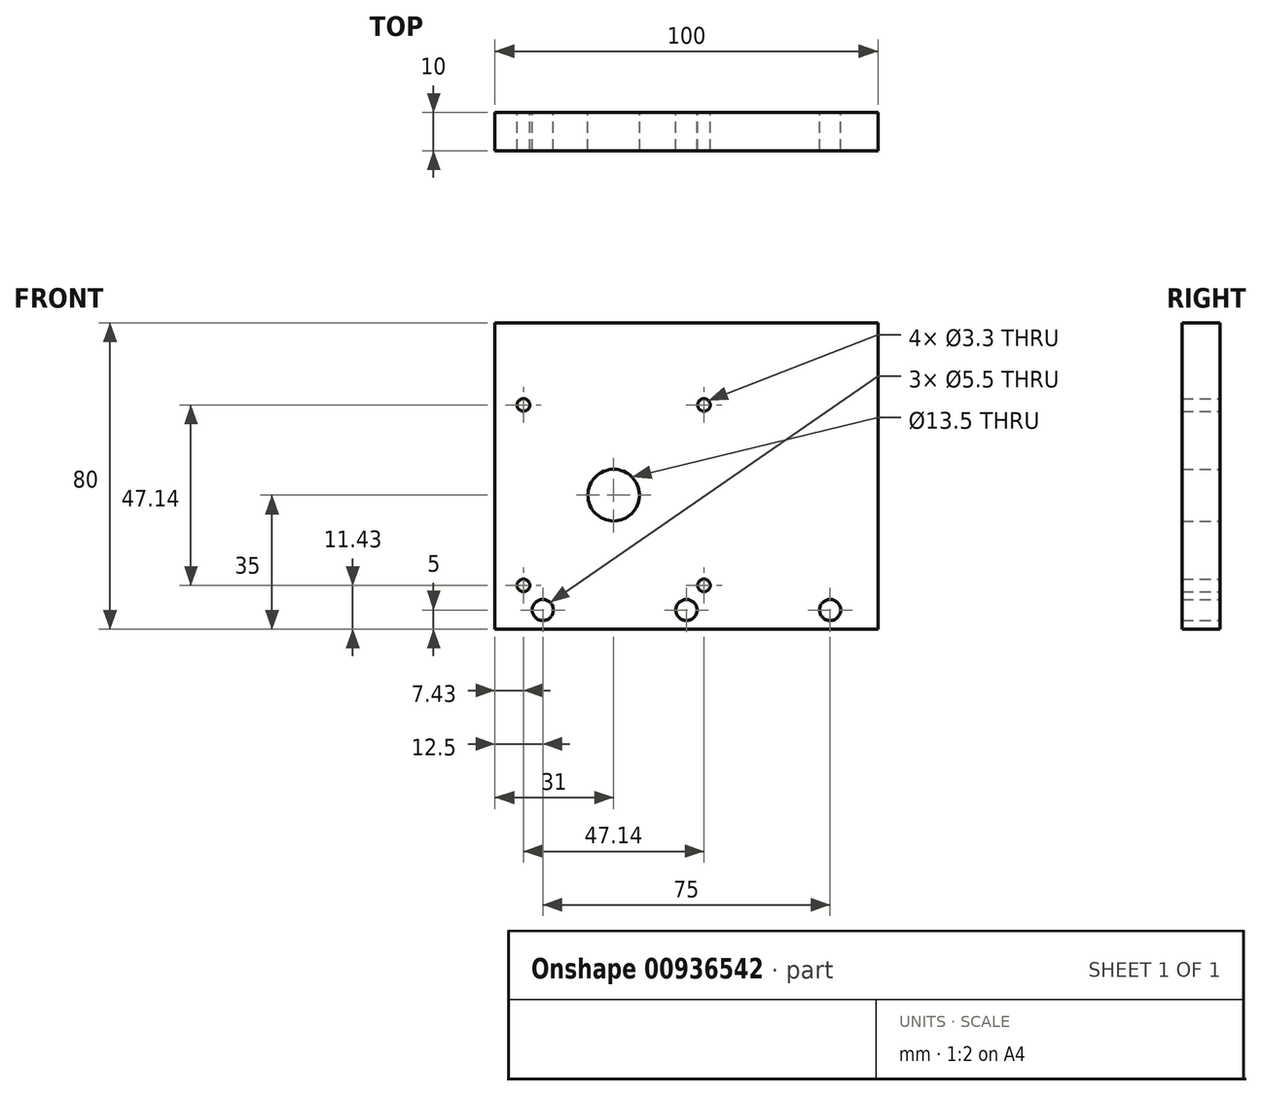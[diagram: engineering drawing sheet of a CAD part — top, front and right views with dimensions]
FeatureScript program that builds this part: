
annotation { "Feature Type Name" : "Feature", "Feature Type Description" : "" }
export const myFeature = defineFeature(function(context is Context, id is Id, definition is map)
    precondition{}
    {
        {
            var Q0;
            Q0=qCreatedBy(makeId("Front.planeOp"),FACE);
            var sketch = newSketch(context, id + "F0", { "sketchPlane" : qUnion([Q0])});
            skLineSegment(sketch, "E0.bottom", {"start": v(50, 40) * mm, "end": v(-50, 40) * mm});
            skLineSegment(sketch, "E0.top", {"start": v(50, -40) * mm, "end": v(-50, -40) * mm});
            skLineSegment(sketch, "E0.left", {"start": v(50, 40) * mm, "end": v(50, -40) * mm});
            skLineSegment(sketch, "E0.right", {"start": v(-50, 40) * mm, "end": v(-50, -40) * mm});
            skPoint(sketch, "E0.middle", {"position": v(0, 0) * mm});
            skSolve(sketch);
        }
        {
            var Q0;
            Q0=makeQuery(id+"F0.imprint","IMPRINT",FACE,{"disambiguationData":[TD([[makeQuery(id+"F0.imprint","IMPRINT",EDGE,{"derivedFrom":sQuery(id+"F0.wireOp",EDGE,"E0.bottom")}),1.0]])]});
            extrude(context, id + "F1", {"entities" : qUnion([Q0]), "depth" : 10 * mm, "offsetDistance" : 25 * mm});
        }
        {
            var Q0;
            Q0=makeQuery(id+"F1.opExtrude","CAP_FACE",FACE,{"disambiguationData":[OSD([sQuery(id+"F0.wireOp",EDGE,"E0.bottom"),sQuery(id+"F0.wireOp",EDGE,"E0.top"),sQuery(id+"F0.wireOp",EDGE,"E0.left"),sQuery(id+"F0.wireOp",EDGE,"E0.right")])],"isStart":false});
            var sketch = newSketch(context, id + "F2", { "sketchPlane" : qUnion([Q0])});
            skLineSegment(sketch, "E1.bottom", {"start": v(4.57, 18.57) * mm, "end": v(-42.57, 18.57) * mm, "construction": true});
            skLineSegment(sketch, "E1.top", {"start": v(4.57, -28.57) * mm, "end": v(-42.57, -28.57) * mm, "construction": true});
            skLineSegment(sketch, "E1.left", {"start": v(4.57, 18.57) * mm, "end": v(4.57, -28.57) * mm, "construction": true});
            skLineSegment(sketch, "E1.right", {"start": v(-42.57, 18.57) * mm, "end": v(-42.57, -28.57) * mm, "construction": true});
            skPoint(sketch, "E1.middle", {"position": v(-19, -5) * mm});
            skPoint(sketch, "E2", {"position": v(4.57, 18.57) * mm});
            skPoint(sketch, "E3", {"position": v(-42.57, 18.57) * mm});
            skPoint(sketch, "E4", {"position": v(-42.57, -28.57) * mm});
            skPoint(sketch, "E5", {"position": v(4.57, -28.57) * mm});
            skLineSegment(sketch, "E6", {"start": v(-50, -35) * mm, "end": v(50, -35) * mm, "construction": true});
            skPoint(sketch, "E7", {"position": v(0, -35) * mm});
            skPoint(sketch, "E8", {"position": v(-37.5, -35) * mm});
            skPoint(sketch, "E9", {"position": v(37.5, -35) * mm});
            skSolve(sketch);
        }
        {
            var Q0;
            Q0=sQuery(id+"F2.wireOp",VERTEX,"E1.bottom.end");
            var Q1;
            Q1=sQuery(id+"F2.wireOp",VERTEX,"E1.bottom.start");
            var Q2;
            Q2=sQuery(id+"F2.wireOp",VERTEX,"E4");
            var Q3;
            Q3=sQuery(id+"F2.wireOp",VERTEX,"E5");
            var Q4;
            Q4=makeQuery(id+"F1.opExtrude","SWEPT_BODY",BODY,{"disambiguationData":[OSD([sQuery(id+"F0.wireOp",EDGE,"E0.bottom"),sQuery(id+"F0.wireOp",EDGE,"E0.top"),sQuery(id+"F0.wireOp",EDGE,"E0.left"),sQuery(id+"F0.wireOp",EDGE,"E0.right")])]});
            hole(context, id + "F3", {"style" : HoleStyle.SIMPLE, "endStyle" : HoleEndStyle.THROUGH, "standardTappedOrClearance" : lookupTablePath({ "standard" : "ISO", "engagement" : "75%", "pitch" : "0.7 mm", "size" : "M4", "type" : "Tapped" }), "standardBlindInLast" : lookupTablePath({ "standard" : "ISO", "fit" : "Normal", "engagement" : "75%", "pitch" : "0.7 mm", "size" : "M4", "type" : "Clearance & tapped" }), "holeDiameter" : 3.3 * mm, "majorDiameter" : 4 * mm, "showTappedDepth" : true, "tappedDepth" : 12 * mm, "tapClearance" : 3, "locations" : qUnion([Q0, Q1, Q2, Q3]), "scope" : qUnion([Q4]), "startStyle" : HoleStartStyle.PART});
        }
        {
            var Q0;
            Q0=sQuery(id+"F2.wireOp",VERTEX,"E1.middle");
            var Q1;
            Q1=makeQuery(id+"F1.opExtrude","SWEPT_BODY",BODY,{"disambiguationData":[OSD([sQuery(id+"F0.wireOp",EDGE,"E0.bottom"),sQuery(id+"F0.wireOp",EDGE,"E0.top"),sQuery(id+"F0.wireOp",EDGE,"E0.left"),sQuery(id+"F0.wireOp",EDGE,"E0.right")])]});
            hole(context, id + "F4", {"style" : HoleStyle.SIMPLE, "endStyle" : HoleEndStyle.THROUGH, "standardTappedOrClearance" : lookupTablePath({ "fit" : "Normal", "standard" : "ISO", "size" : "M12", "type" : "Clearance" }), "standardBlindInLast" : lookupTablePath({ "fit" : "Normal", "standard" : "ISO", "engagement" : "75%", "pitch" : "1.75 mm", "size" : "M12", "type" : "Clearance & tapped" }), "holeDiameter" : 13.5 * mm, "majorDiameter" : 4 * mm, "tappedDepth" : 12 * mm, "tapClearance" : 3, "locations" : qUnion([Q0]), "scope" : qUnion([Q1]), "startStyle" : HoleStartStyle.PART});
        }
        {
            var Q0;
            Q0=sQuery(id+"F2.wireOp",VERTEX,"E8");
            var Q1;
            Q1=sQuery(id+"F2.wireOp",VERTEX,"E7");
            var Q2;
            Q2=sQuery(id+"F2.wireOp",VERTEX,"E9");
            var Q3;
            Q3=makeQuery(id+"F1.opExtrude","SWEPT_BODY",BODY,{"disambiguationData":[OSD([sQuery(id+"F0.wireOp",EDGE,"E0.bottom"),sQuery(id+"F0.wireOp",EDGE,"E0.top"),sQuery(id+"F0.wireOp",EDGE,"E0.left"),sQuery(id+"F0.wireOp",EDGE,"E0.right")])]});
            hole(context, id + "F5", {"style" : HoleStyle.SIMPLE, "endStyle" : HoleEndStyle.BLIND, "standardTappedOrClearance" : lookupTablePath({ "fit" : "Normal", "standard" : "ISO", "size" : "M5", "type" : "Clearance" }), "standardBlindInLast" : lookupTablePath({ "fit" : "Normal", "standard" : "ISO", "engagement" : "75%", "pitch" : "0.8 mm", "size" : "M5", "type" : "Clearance & tapped" }), "holeDiameter" : 5.5 * mm, "majorDiameter" : 5 * mm, "holeDepth" : 14.4 * mm, "tappedDepth" : 12 * mm, "tapClearance" : 3, "locations" : qUnion([Q0, Q1, Q2]), "scope" : qUnion([Q3]), "startStyle" : HoleStartStyle.PART});
        }
    });
